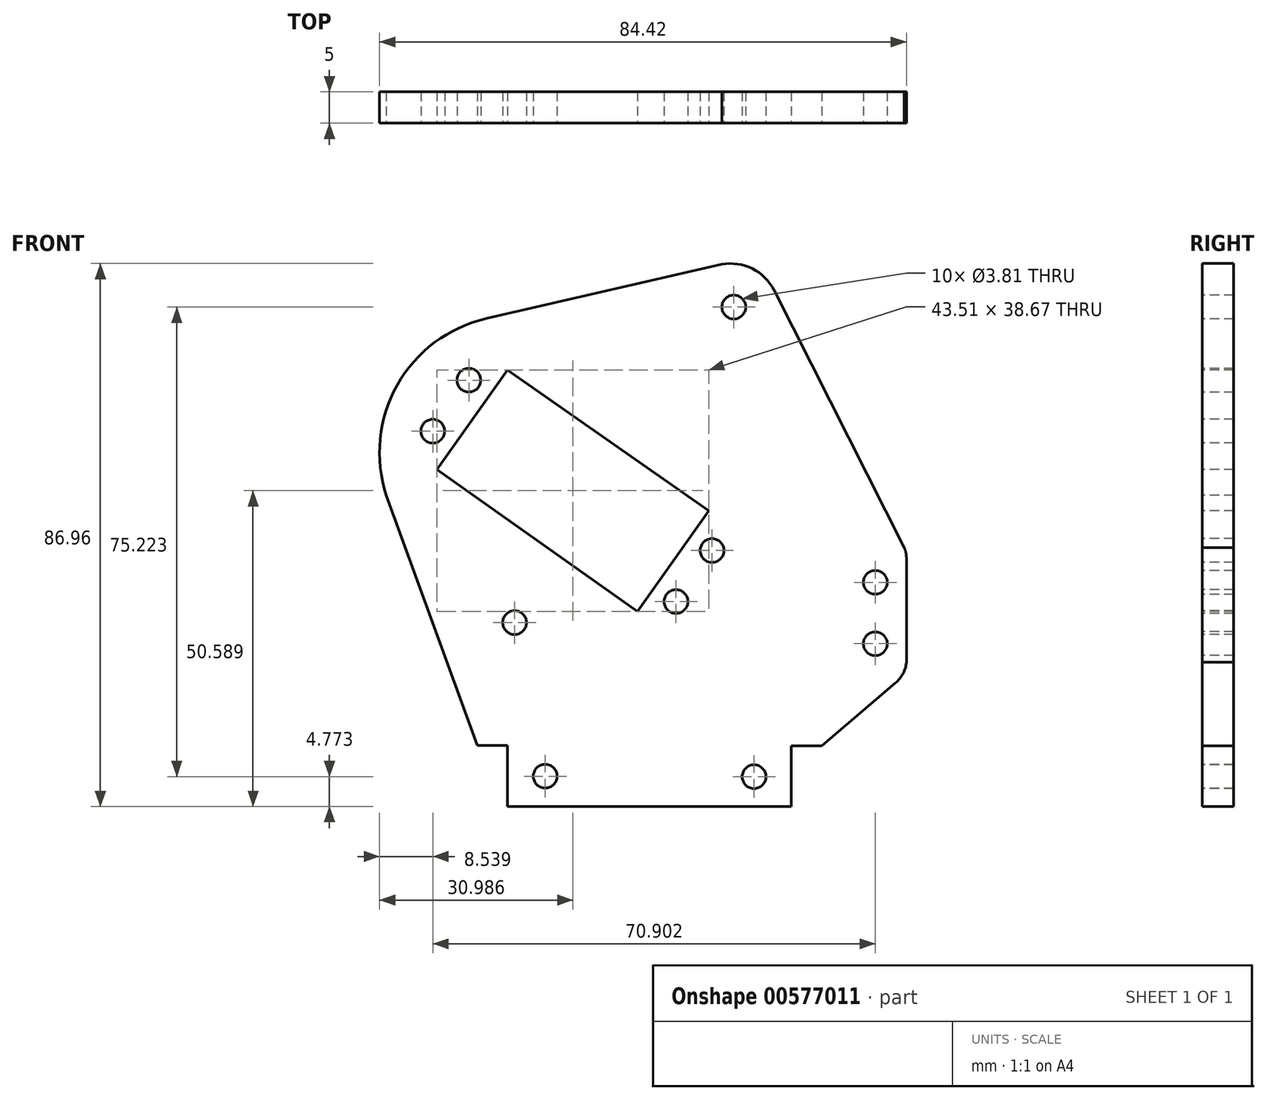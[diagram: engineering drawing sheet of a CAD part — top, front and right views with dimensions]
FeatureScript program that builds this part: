
annotation { "Feature Type Name" : "Feature", "Feature Type Description" : "" }
export const myFeature = defineFeature(function(context is Context, id is Id, definition is map)
    precondition{}
    {
        {
            var Q0;
            Q0=qCreatedBy(makeId("Front.planeOp"),FACE);
            var sketch = newSketch(context, id + "F0", { "sketchPlane" : qUnion([Q0])});
            skLineSegment(sketch, "E0", {"start": v(19.64, 89.45) * mm, "end": v(19.64, 79.72) * mm});
            skLineSegment(sketch, "E1", {"start": v(19.64, 79.72) * mm, "end": v(14.76, 79.72) * mm});
            skLineSegment(sketch, "E2", {"start": v(14.76, 79.72) * mm, "end": v(2.94, 69.65) * mm});
            skLineSegment(sketch, "E3", {"start": v(19.64, 89.45) * mm, "end": v(65.11, 89.45) * mm});
            skLineSegment(sketch, "E4", {"start": v(65.11, 89.45) * mm, "end": v(65.11, 79.7) * mm});
            skLineSegment(sketch, "E5", {"start": v(65.11, 79.7) * mm, "end": v(69.98, 79.7) * mm});
            skLineSegment(sketch, "E6", {"start": v(69.98, 79.7) * mm, "end": v(84.53, 39.63) * mm});
            skLineSegment(sketch, "E7", {"start": v(30.78, 2.62) * mm, "end": v(68.54, 11.3) * mm});
            skLineSegment(sketch, "E8", {"start": v(1.21, 66.37) * mm, "end": v(1.21, 49.52) * mm});
            skLineSegment(sketch, "E9", {"start": v(1.56, 48) * mm, "end": v(22.4, 6.78) * mm});
            skArc(sketch, "E10", {"start": v(2.94, 69.65) * mm, "mid": v(1.76, 68.18) * mm, "end": v(1.21, 66.37) * mm});
            skArc(sketch, "E11", {"start": v(1.21, 49.52) * mm, "mid": v(1.3, 48.74) * mm, "end": v(1.56, 48) * mm});
            skArc(sketch, "E12", {"start": v(22.4, 6.78) * mm, "mid": v(25.9, 3.3) * mm, "end": v(30.78, 2.62) * mm});
            skArc(sketch, "E13", {"start": v(68.54, 11.3) * mm, "mid": v(82.78, 21.95) * mm, "end": v(84.53, 39.63) * mm});
            skLineSegment(sketch, "E14", {"start": v(32.89, 42.1) * mm, "end": v(44.27, 58.2) * mm});
            skLineSegment(sketch, "E15", {"start": v(44.27, 58.2) * mm, "end": v(76.4, 35.49) * mm});
            skLineSegment(sketch, "E16", {"start": v(76.4, 35.49) * mm, "end": v(65.11, 19.52) * mm});
            skLineSegment(sketch, "E17", {"start": v(65.11, 19.52) * mm, "end": v(32.89, 42.1) * mm});
            skCircle(sketch, "E18", {"center": v(38.12, 56.63) * mm, "radius": 1.9 * mm});
            skPoint(sketch, "E18.first.point", {"position": v(38.07, 58.53) * mm});
            skPoint(sketch, "E18.second.point", {"position": v(40.02, 56.8) * mm});
            skPoint(sketch, "E18.third.point", {"position": v(36.96, 55.12) * mm});
            skCircle(sketch, "E19", {"center": v(32.35, 48.46) * mm, "radius": 1.9 * mm});
            skPoint(sketch, "E19.first.point", {"position": v(32.68, 46.58) * mm});
            skPoint(sketch, "E19.second.point", {"position": v(32.7, 50.33) * mm});
            skPoint(sketch, "E19.third.point", {"position": v(30.65, 49.32) * mm});
            skCircle(sketch, "E20", {"center": v(6.2, 63.38) * mm, "radius": 1.9 * mm});
            skPoint(sketch, "E20.first.point", {"position": v(6.19, 65.29) * mm});
            skPoint(sketch, "E20.second.point", {"position": v(8.1, 63.37) * mm});
            skPoint(sketch, "E20.third.point", {"position": v(5.37, 61.67) * mm});
            skCircle(sketch, "E21", {"center": v(6.19, 53.55) * mm, "radius": 1.9 * mm});
            skPoint(sketch, "E21.first.point", {"position": v(5.44, 55.3) * mm});
            skPoint(sketch, "E21.second.point", {"position": v(8.1, 53.49) * mm});
            skPoint(sketch, "E21.third.point", {"position": v(6.06, 51.65) * mm});
            skCircle(sketch, "E22", {"center": v(28.86, 9.45) * mm, "radius": 1.9 * mm});
            skCircle(sketch, "E23", {"center": v(71.31, 21.17) * mm, "radius": 1.9 * mm});
            skCircle(sketch, "E24", {"center": v(77.1, 29.34) * mm, "radius": 1.9 * mm});
            skCircle(sketch, "E25", {"center": v(63.99, 60) * mm, "radius": 1.9 * mm});
            skCircle(sketch, "E26", {"center": v(59.08, 84.6) * mm, "radius": 1.9 * mm});
            skCircle(sketch, "E27", {"center": v(25.62, 84.68) * mm, "radius": 1.9 * mm});
            skCircle(sketch, "E28.MirrorC", {"center": v(-32.35, 48.46) * mm, "radius": 1.9 * mm});
            skLineSegment(sketch, "E29.MirrorCS", {"start": v(-65.11, 79.7) * mm, "end": v(-69.98, 79.7) * mm});
            skLineSegment(sketch, "E30.MirrorCS", {"start": v(-19.64, 79.72) * mm, "end": v(-14.76, 79.72) * mm});
            skArc(sketch, "E31.MirrorCS", {"start": v(-1.21, 49.52) * mm, "mid": v(-1.3, 48.74) * mm, "end": v(-1.56, 48) * mm});
            skArc(sketch, "E32.MirrorCS", {"start": v(-2.94, 69.65) * mm, "mid": v(-1.76, 68.18) * mm, "end": v(-1.21, 66.37) * mm});
            skCircle(sketch, "E33.MirrorC", {"center": v(-38.12, 56.63) * mm, "radius": 1.9 * mm});
            skCircle(sketch, "E34.MirrorC", {"center": v(-6.19, 53.55) * mm, "radius": 1.9 * mm});
            skCircle(sketch, "E35.MirrorC", {"center": v(-59.08, 84.6) * mm, "radius": 1.9 * mm});
            skCircle(sketch, "E36.MirrorC", {"center": v(-6.2, 63.38) * mm, "radius": 1.9 * mm});
            skCircle(sketch, "E37.MirrorC", {"center": v(-77.1, 29.34) * mm, "radius": 1.9 * mm});
            skCircle(sketch, "E38.MirrorC", {"center": v(-71.31, 21.17) * mm, "radius": 1.9 * mm});
            skCircle(sketch, "E39.MirrorC", {"center": v(-28.86, 9.45) * mm, "radius": 1.9 * mm});
            skPoint(sketch, "E40.MirrorP", {"position": v(-6.19, 65.29) * mm});
            skLineSegment(sketch, "E41.MirrorCS", {"start": v(-32.89, 42.1) * mm, "end": v(-44.27, 58.2) * mm});
            skCircle(sketch, "E42.MirrorC", {"center": v(-25.62, 84.68) * mm, "radius": 1.9 * mm});
            skPoint(sketch, "E43.MirrorP", {"position": v(-40.02, 56.8) * mm});
            skPoint(sketch, "E44.MirrorP", {"position": v(-32.7, 50.33) * mm});
            skPoint(sketch, "E45.MirrorP", {"position": v(-6.06, 51.65) * mm});
            skArc(sketch, "E46.MirrorCS", {"start": v(-68.54, 11.3) * mm, "mid": v(-82.78, 21.95) * mm, "end": v(-84.53, 39.63) * mm});
            skLineSegment(sketch, "E47.MirrorCS", {"start": v(-65.11, 19.52) * mm, "end": v(-32.89, 42.1) * mm});
            skPoint(sketch, "E48.MirrorP", {"position": v(-38.07, 58.53) * mm});
            skPoint(sketch, "E49.MirrorP", {"position": v(-32.68, 46.58) * mm});
            skPoint(sketch, "E50.MirrorP", {"position": v(-8.1, 53.49) * mm});
            skPoint(sketch, "E51.MirrorP", {"position": v(-30.65, 49.32) * mm});
            skArc(sketch, "E52.MirrorCS", {"start": v(-22.4, 6.78) * mm, "mid": v(-25.9, 3.3) * mm, "end": v(-30.78, 2.62) * mm});
            skCircle(sketch, "E53.MirrorC", {"center": v(-63.99, 60) * mm, "radius": 1.9 * mm});
            skPoint(sketch, "E54.MirrorP", {"position": v(-5.37, 61.67) * mm});
            skLineSegment(sketch, "E55.MirrorCS", {"start": v(-76.4, 35.49) * mm, "end": v(-65.11, 19.52) * mm});
            skLineSegment(sketch, "E56.MirrorCS", {"start": v(-1.21, 66.37) * mm, "end": v(-1.21, 49.52) * mm});
            skLineSegment(sketch, "E57.MirrorCS", {"start": v(-30.78, 2.62) * mm, "end": v(-68.54, 11.3) * mm});
            skLineSegment(sketch, "E58.MirrorCS", {"start": v(-69.98, 79.7) * mm, "end": v(-84.53, 39.63) * mm});
            skLineSegment(sketch, "E59.MirrorCS", {"start": v(-65.11, 89.45) * mm, "end": v(-65.11, 79.7) * mm});
            skLineSegment(sketch, "E60.MirrorCS", {"start": v(-19.64, 89.45) * mm, "end": v(-65.11, 89.45) * mm});
            skLineSegment(sketch, "E61.MirrorCS", {"start": v(-14.76, 79.72) * mm, "end": v(-2.94, 69.65) * mm});
            skLineSegment(sketch, "E62.MirrorCS", {"start": v(-19.64, 89.45) * mm, "end": v(-19.64, 79.72) * mm});
            skPoint(sketch, "E63.MirrorP", {"position": v(-5.44, 55.3) * mm});
            skLineSegment(sketch, "E64.MirrorCS", {"start": v(-44.27, 58.2) * mm, "end": v(-76.4, 35.49) * mm});
            skLineSegment(sketch, "E65.MirrorCS", {"start": v(-1.56, 48) * mm, "end": v(-22.4, 6.78) * mm});
            skPoint(sketch, "E66.MirrorP", {"position": v(-8.1, 63.37) * mm});
            skPoint(sketch, "E67.MirrorP", {"position": v(-36.96, 55.12) * mm});
            skLineSegment(sketch, "E68.MirrorCS", {"start": v(-19.64, -79.72) * mm, "end": v(-14.76, -79.72) * mm});
            skLineSegment(sketch, "E69.MirrorCS", {"start": v(-65.11, -79.7) * mm, "end": v(-69.98, -79.7) * mm});
            skArc(sketch, "E70.MirrorCS", {"start": v(-2.94, -69.65) * mm, "mid": v(-1.76, -68.18) * mm, "end": v(-1.21, -66.37) * mm});
            skArc(sketch, "E71.MirrorCS", {"start": v(-1.21, -49.52) * mm, "mid": v(-1.3, -48.74) * mm, "end": v(-1.56, -48) * mm});
            skCircle(sketch, "E72.MirrorC", {"center": v(-77.1, -29.34) * mm, "radius": 1.9 * mm});
            skCircle(sketch, "E73.MirrorC", {"center": v(-6.2, -63.38) * mm, "radius": 1.9 * mm});
            skCircle(sketch, "E74.MirrorC", {"center": v(-32.35, -48.46) * mm, "radius": 1.9 * mm});
            skCircle(sketch, "E75.MirrorC", {"center": v(-28.86, -9.45) * mm, "radius": 1.9 * mm});
            skCircle(sketch, "E76.MirrorC", {"center": v(-38.12, -56.63) * mm, "radius": 1.9 * mm});
            skCircle(sketch, "E77.MirrorC", {"center": v(-6.19, -53.55) * mm, "radius": 1.9 * mm});
            skLineSegment(sketch, "E78.MirrorCS", {"start": v(-76.4, -35.49) * mm, "end": v(-65.11, -19.52) * mm});
            skLineSegment(sketch, "E79.MirrorCS", {"start": v(-19.64, -89.45) * mm, "end": v(-19.64, -79.72) * mm});
            skPoint(sketch, "E80.MirrorP", {"position": v(-8.1, -63.37) * mm});
            skPoint(sketch, "E81.MirrorP", {"position": v(-6.06, -51.65) * mm});
            skCircle(sketch, "E82.MirrorC", {"center": v(-63.99, -60) * mm, "radius": 1.9 * mm});
            skLineSegment(sketch, "E83.MirrorCS", {"start": v(-14.76, -79.72) * mm, "end": v(-2.94, -69.65) * mm});
            skPoint(sketch, "E84.MirrorP", {"position": v(-5.44, -55.3) * mm});
            skArc(sketch, "E85.MirrorCS", {"start": v(-22.4, -6.78) * mm, "mid": v(-25.9, -3.3) * mm, "end": v(-30.78, -2.62) * mm});
            skPoint(sketch, "E86.MirrorP", {"position": v(-5.37, -61.67) * mm});
            skCircle(sketch, "E87.MirrorC", {"center": v(-59.08, -84.6) * mm, "radius": 1.9 * mm});
            skLineSegment(sketch, "E88.MirrorCS", {"start": v(-19.64, -89.45) * mm, "end": v(-65.11, -89.45) * mm});
            skPoint(sketch, "E89.MirrorP", {"position": v(-32.7, -50.33) * mm});
            skLineSegment(sketch, "E90.MirrorCS", {"start": v(-32.89, -42.1) * mm, "end": v(-44.27, -58.2) * mm});
            skPoint(sketch, "E91.MirrorP", {"position": v(-32.68, -46.58) * mm});
            skCircle(sketch, "E92.MirrorC", {"center": v(-25.62, -84.68) * mm, "radius": 1.9 * mm});
            skLineSegment(sketch, "E93.MirrorCS", {"start": v(-30.78, -2.62) * mm, "end": v(-68.54, -11.3) * mm});
            skLineSegment(sketch, "E94.MirrorCS", {"start": v(-1.56, -48) * mm, "end": v(-22.4, -6.78) * mm});
            skPoint(sketch, "E95.MirrorP", {"position": v(-6.19, -65.29) * mm});
            skPoint(sketch, "E96.MirrorP", {"position": v(-30.65, -49.32) * mm});
            skPoint(sketch, "E97.MirrorP", {"position": v(-38.07, -58.53) * mm});
            skLineSegment(sketch, "E98.MirrorCS", {"start": v(-1.21, -66.37) * mm, "end": v(-1.21, -49.52) * mm});
            skCircle(sketch, "E99.MirrorC", {"center": v(-71.31, -21.17) * mm, "radius": 1.9 * mm});
            skLineSegment(sketch, "E100.MirrorCS", {"start": v(-44.27, -58.2) * mm, "end": v(-76.4, -35.49) * mm});
            skPoint(sketch, "E101.MirrorP", {"position": v(-36.96, -55.12) * mm});
            skLineSegment(sketch, "E102.MirrorCS", {"start": v(-65.11, -19.52) * mm, "end": v(-32.89, -42.1) * mm});
            skPoint(sketch, "E103.MirrorP", {"position": v(-8.1, -53.49) * mm});
            skArc(sketch, "E104.MirrorCS", {"start": v(-68.54, -11.3) * mm, "mid": v(-82.78, -21.95) * mm, "end": v(-84.53, -39.63) * mm});
            skPoint(sketch, "E105.MirrorP", {"position": v(-40.02, -56.8) * mm});
            skLineSegment(sketch, "E106.MirrorCS", {"start": v(-65.11, -89.45) * mm, "end": v(-65.11, -79.7) * mm});
            skLineSegment(sketch, "E107.MirrorCS", {"start": v(-69.98, -79.7) * mm, "end": v(-84.53, -39.63) * mm});
            skSolve(sketch);
        }
        {
            var Q0;
            Q0=makeQuery(id+"F0.imprint","IMPRINT",FACE,{"disambiguationData":[TD([[makeQuery(id+"F0.imprint","IMPRINT",EDGE,{"derivedFrom":sQuery(id+"F0.wireOp",EDGE,"E68.MirrorCS")}),1.0]])]});
            extrude(context, id + "F1", {"entities" : qUnion([Q0]), "oppositeDirection" : true, "depth" : 5 * mm, "offsetDistance" : 25.4 * mm});
        }
    });
